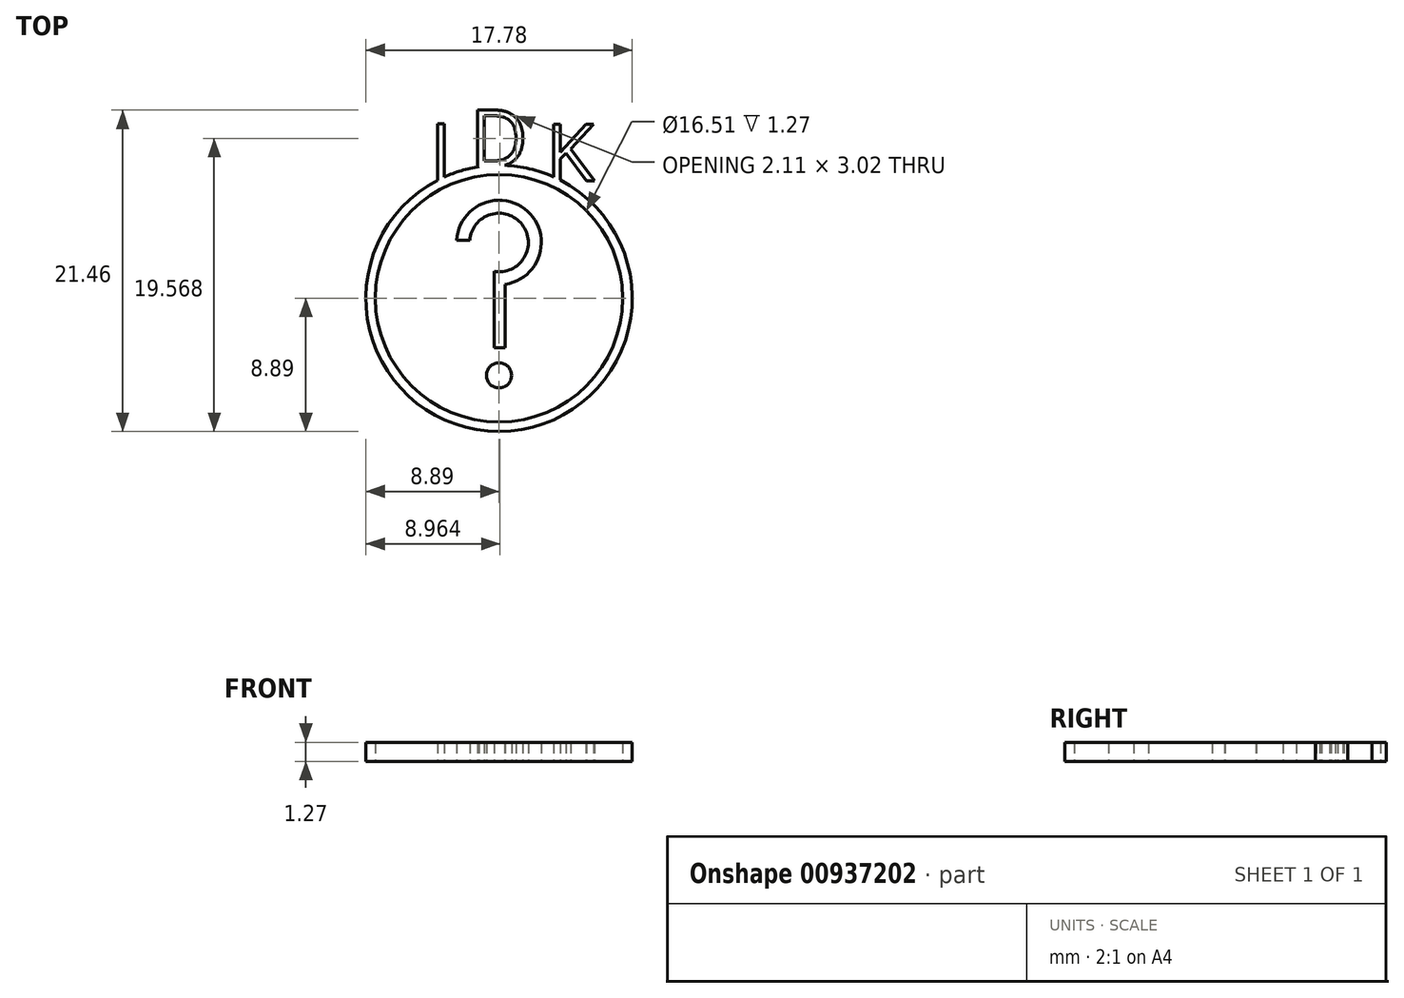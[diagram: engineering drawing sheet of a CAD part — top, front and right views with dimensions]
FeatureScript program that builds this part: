
annotation { "Feature Type Name" : "Feature", "Feature Type Description" : "" }
export const myFeature = defineFeature(function(context is Context, id is Id, definition is map)
    precondition{}
    {
        {
            var Q0;
            Q0=qCreatedBy(makeId("Top.planeOp"),FACE);
            var sketch = newSketch(context, id + "F0", { "sketchPlane" : qUnion([Q0])});
            skCircle(sketch, "E0", {"center": v(0, 0) * mm, "radius": 8.9 * mm});
            skText(sketch, "E1", { "text": "I\n", "fontName": "OpenSans-Regular.ttf"});
            skText(sketch, "E2", { "text": "D", "fontName": "OpenSans-Regular.ttf"});
            skText(sketch, "E3", { "text": "K\n", "fontName": "OpenSans-Regular.ttf"});
            skCircle(sketch, "E4", {"center": v(0, 0) * mm, "radius": 8.26 * mm});
            skLineSegment(sketch, "E5.top", {"start": v(-0.33, -3.31) * mm, "end": v(0.42, -3.31) * mm});
            skLineSegment(sketch, "E5.left", {"start": v(-0.33, 1.93) * mm, "end": v(-0.33, -3.31) * mm});
            skLineSegment(sketch, "E5.right", {"start": v(0.42, 1.93) * mm, "end": v(0.42, 1.82) * mm});
            skCircle(sketch, "E6", {"center": v(0, -5.15) * mm, "radius": 0.84 * mm});
            skArc(sketch, "E7", {"start": v(0.42, 0.93) * mm, "mid": v(1.9, 5.82) * mm, "end": v(-2.82, 3.87) * mm});
            skArc(sketch, "E8", {"start": v(-0.33, 1.8) * mm, "mid": v(1.54, 4.93) * mm, "end": v(-1.95, 3.88) * mm});
            skPoint(sketch, "E9", {"position": v(-2.82, 3.87) * mm});
            skPoint(sketch, "E10", {"position": v(-1.95, 3.88) * mm});
            skPoint(sketch, "E11", {"position": v(-0.33, 0.92) * mm});
            skPoint(sketch, "E12", {"position": v(0.42, 0.93) * mm});
            skLineSegment(sketch, "E13.trimOffspring", {"start": v(0.42, 0.93) * mm, "end": v(0.42, -3.31) * mm});
            skLineSegment(sketch, "E14", {"start": v(-2.82, 3.87) * mm, "end": v(-1.95, 3.88) * mm});
            const initialGuessF0  = {"E1": [-0.00462, 0.00788, 1, 0, 0.0038], "E2": [-0.00194, 0.00879, 1, 0, 0.00381], "E3": [0.00312, 0.00784, 1, 0, 0.00381]};
            skSetInitialGuess(sketch, initialGuessF0);
            skSolve(sketch);
        }
        {
            var Q0;
            Q0 = qSketchRegion(id + "F0", true);
            extrude(context, id + "F1", {"entities" : qUnion([Q0]), "depth" : 1.27 * mm, "offsetDistance" : 25.4 * mm});
        }
        {
            var Q0;
            {var subQ4=sQuery(id+"F0.wireOp",EDGE,"E5.top");Q0=makeQuery(id+"F0.imprint","IMPRINT",FACE,{"disambiguationData":[TD([[makeQuery(id+"F0.imprint","IMPRINT",EDGE,{"derivedFrom":subQ4}),1.0]])]});}
            var Q1;
            Q1=makeQuery(id+"F0.imprint","IMPRINT",FACE,{"disambiguationData":[TD([[makeQuery(id+"F0.imprint","IMPRINT",EDGE,{"derivedFrom":sQuery(id+"F0.wireOp",EDGE,"E6")}),1.0]])]});
            extrude(context, id + "F2", {"entities" : qUnion([Q0, Q1]), "depth" : 1.27 * mm, "offsetDistance" : 25.4 * mm});
        }
    });
